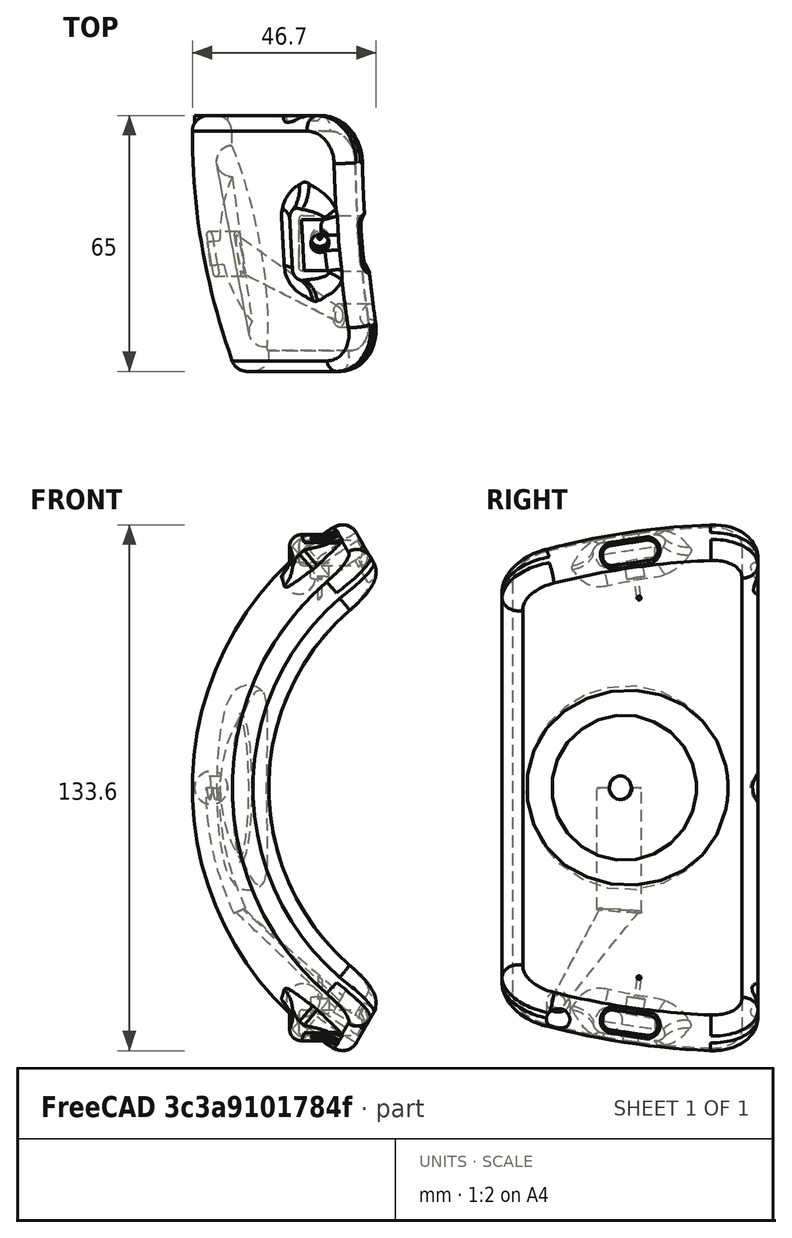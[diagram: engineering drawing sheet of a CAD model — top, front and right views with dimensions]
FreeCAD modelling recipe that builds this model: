
FCSTD DOCUMENT  (FreeCAD 0.17R13541 (Git))
Label: right_patch_backup
License: All rights reserved
LicenseURL: http://en.wikipedia.org/wiki/All_rights_reserved
objects: PartDesign::Fillet×12, Sketcher::SketchObject×11, PartDesign::Pocket×4, PartDesign::Mirrored×4, PartDesign::Revolution×1, PartDesign::Line×1, PartDesign::SubtractiveSphere×1, PartDesign::SubtractiveTorus×1, PartDesign::SubtractiveCylinder×1, PartDesign::AdditiveLoft×1, PartDesign::Plane×1, PartDesign::Body×1, PartDesign::Groove×1, PartDesign::SubtractiveLoft×1, PartDesign::Pad×1
note: 54 computed .brp shape members not serialized (recipe doc carries the construction recipe); baked Part::Feature solids carry a one-line shape summary decoded from their .brp

FEATURE [Sketcher::SketchObject] Sketch
  MapMode = 5
  Support = -> [XY_Plane]
  sketch-geometry (14):
    g0: LineSegment StartX=-68 StartY=0 StartZ=0 EndX=-58 EndY=0 EndZ=0
    g1: LineSegment StartX=-79 StartY=65 StartZ=0 EndX=-69 EndY=65 EndZ=0
    g2: Circle [constr] CenterX=-79 CenterY=65 CenterZ=0 NormalX=0 NormalY=0 NormalZ=1 AngleXU=0 Radius=1
    g3: Circle [constr] CenterX=-80 CenterY=32.5 CenterZ=0 NormalX=0 NormalY=0 NormalZ=1 AngleXU=0 Radius=1
    g4: Circle [constr] CenterX=-68 CenterY=0 CenterZ=0 NormalX=0 NormalY=0 NormalZ=1 AngleXU=0 Radius=1
    g5: BSplineCurve PolesCount=3 KnotsCount=2 Degree=2 IsPeriodic=0
    g6: GeomPoint [constr] X=-79 Y=65 Z=0
    g7: GeomPoint [constr] X=-68 Y=0 Z=0
    g8: Circle [constr] CenterX=-69 CenterY=65 CenterZ=0 NormalX=0 NormalY=0 NormalZ=1 AngleXU=0 Radius=1
    g9: Circle [constr] CenterX=-70 CenterY=32.5 CenterZ=0 NormalX=0 NormalY=0 NormalZ=1 AngleXU=0 Radius=1
    g10: Circle [constr] CenterX=-58 CenterY=0 CenterZ=0 NormalX=0 NormalY=0 NormalZ=1 AngleXU=0 Radius=1
    g11: BSplineCurve PolesCount=3 KnotsCount=2 Degree=2 IsPeriodic=0
    g12: GeomPoint [constr] X=-69 Y=65 Z=0
    g13: GeomPoint [constr] X=-58 Y=0 Z=0
  constraints (32):
    c: Horizontal(g0)
    c: Horizontal(g1)
    c: Coincident(g2,g1)
    c: Radius(g2) = 1
    c: Equal(g2,g3)
    c: Equal(g2,g4)
    c: Coincident(g4,g0)
    c: InternalAlignment(g2,g5)
    c: InternalAlignment(g3,g5)
    c: InternalAlignment(g4,g5)
    c: InternalAlignment(g6,g5)
    c: InternalAlignment(g7,g5)
    c: Coincident(g8,g1)
    c: Radius(g8) = 1
    c: Equal(g8,g9)
    c: Equal(g8,g10)
    c: Coincident(g10,g0)
    c: InternalAlignment(g8,g11)
    c: InternalAlignment(g9,g11)
    c: InternalAlignment(g10,g11)
    c: InternalAlignment(g12,g11)
    c: InternalAlignment(g13,g11)
    c: DistanceX(g1,g1) = 10
    c: DistanceX(g0,g0) = 10
    c: DistanceY(g0,g1) = 65
    c: DistanceY(g0,g-1) = 0
    c: DistanceY(g0,g9) = 32.5
    c: DistanceY(g0,g3) = 32.5
    c: DistanceX(g0,g-1) = 58
    c: DistanceX(g3,g9) = 10
    c: DistanceX(g9,g0) = 12
    c: DistanceX(g1,g0) = 11
FEATURE [PartDesign::Revolution] Revolution
  Angle = 120
  Axis = (0,1,0)
  Base = (0,0,0)
  Midplane = true
  Profile = -> Sketch
  ReferenceAxis = -> Sketch [V_Axis]
FEATURE [Sketcher::SketchObject] Sketch001
  MapMode = 5
  Support = -> [XY_Plane]
  sketch-geometry (5):
    g0: ArcOfCircle CenterX=-74.7751 CenterY=34.7178 CenterZ=0 NormalX=0 NormalY=0 NormalZ=1 AngleXU=0 Radius=0.75 StartAngle=0.174533 EndAngle=3.31613
    g1: ArcOfCircle CenterX=-73.0386 CenterY=24.8698 CenterZ=0 NormalX=0 NormalY=0 NormalZ=1 AngleXU=0 Radius=0.75 StartAngle=3.31613 EndAngle=6.45772
    g2: LineSegment StartX=-75.5137 StartY=34.5876 StartZ=0 EndX=-73.7772 EndY=24.7395 EndZ=0
    g3: LineSegment StartX=-74.0365 StartY=34.8481 StartZ=0 EndX=-72.3 EndY=25 EndZ=0
    g4: LineSegment [constr] StartX=17.7 StartY=33.8377 StartZ=0 EndX=17.7 EndY=-7.32293 EndZ=0
  constraints (12):
    c: Tangent(g0,g3) = 1.5708
    c: Tangent(g0,g2) = -1.5708
    c: Tangent(g2,g1) = -1.5708
    c: Tangent(g3,g1) = 1.5708
    c: Equal(g0,g1)
    c: Angle(g-1,g3) = 1.74533
    c: Distance(g1,g0) = 10
    c: Distance(g0,g0) = 1.5
    c: DistanceX(g1,g-1) = 72.3
    c: DistanceY(g-1,g1) = 25
    c: Vertical(g4)
    c: DistanceX(g1,g4) = 90
FEATURE [Sketcher::SketchObject] Sketch002
  MapMode = 5
  Placement = pos=(0,23,0) rot=(1,0,0;1.5708rad)
  sketch-geometry (5):
    g0: LineSegment StartX=-54 StartY=63 StartZ=0 EndX=-40 EndY=63 EndZ=0
    g1: LineSegment [constr] StartX=-40 StartY=63 StartZ=0 EndX=-40 EndY=45 EndZ=0
    g2: LineSegment [constr] StartX=-40 StartY=45 StartZ=0 EndX=-54 EndY=45 EndZ=0
    g3: LineSegment StartX=-54 StartY=45 StartZ=0 EndX=-54 EndY=63 EndZ=0
    g4: LineSegment StartX=-54 StartY=45 StartZ=0 EndX=-40 EndY=63 EndZ=0
  constraints (14):
    c: Coincident(g0,g1)
    c: Coincident(g1,g2)
    c: Coincident(g2,g3)
    c: Coincident(g3,g0)
    c: Horizontal(g0)
    c: Horizontal(g2)
    c: Vertical(g1)
    c: Vertical(g3)
    c: DistanceY(g1,g0) = 18
    c: DistanceX(g0,g0) = 14
    c: DistanceX(g1,g-1) = 40
    c: DistanceY(g-1,g0) = 63
    c: Coincident(g4,g0)
    c: Coincident(g4,g2)
FEATURE [Sketcher::SketchObject] Sketch003
  MapMode = 5
  Placement = pos=(0,0,0) rot=(0.57735,0.57735,0.57735;2.0944rad)
  Support = -> [YZ_Plane]
  sketch-geometry (4):
    g0: ArcOfCircle CenterX=28.0189 CenterY=59 CenterZ=0 NormalX=0 NormalY=0 NormalZ=1 AngleXU=0 Radius=2.57832 StartAngle=1.71915 EndAngle=4.86074
    g1: ArcOfCircle CenterX=37.0189 CenterY=60.3451 CenterZ=0 NormalX=0 NormalY=0 NormalZ=1 AngleXU=0 Radius=2.57832 StartAngle=4.86074 EndAngle=8.00233
    g2: LineSegment StartX=28.4 StartY=56.45 StartZ=0 EndX=37.4 EndY=57.7951 EndZ=0
    g3: LineSegment StartX=27.6378 StartY=61.55 StartZ=0 EndX=36.6378 EndY=62.8951 EndZ=0
  constraints (10):
    c: Tangent(g0,g3) = 1.5708
    c: Tangent(g0,g2) = -1.5708
    c: Tangent(g2,g1) = -1.5708
    c: Tangent(g3,g1) = 1.5708
    c: Equal(g0,g1)
    c: DistanceY(g1,g1) = 5.1
    c: DistanceX(g0,g1) = 9
    c: DistanceX(g-1,g0) = 28.4
    c: DistanceY(g-1,g0) = 59
    c: Angle(g3,g-1) = -0.148353
FEATURE [Sketcher::SketchObject] Sketch004
  MapMode = 5
  Placement = pos=(0,42,0) rot=(1,0,0;1.5708rad)
  sketch-geometry (5):
    g0: LineSegment StartX=-54 StartY=65.8 StartZ=0 EndX=-40 EndY=65.8 EndZ=0
    g1: LineSegment [constr] StartX=-40 StartY=65.8 StartZ=0 EndX=-40 EndY=47.8 EndZ=0
    g2: LineSegment [constr] StartX=-40 StartY=47.8 StartZ=0 EndX=-54 EndY=47.8 EndZ=0
    g3: LineSegment StartX=-54 StartY=47.8 StartZ=0 EndX=-54 EndY=65.8 EndZ=0
    g4: LineSegment StartX=-54 StartY=47.8 StartZ=0 EndX=-40 EndY=65.8 EndZ=0
  constraints (14):
    c: Coincident(g0,g1)
    c: Coincident(g1,g2)
    c: Coincident(g2,g3)
    c: Coincident(g3,g0)
    c: Horizontal(g0)
    c: Horizontal(g2)
    c: Vertical(g1)
    c: Vertical(g3)
    c: DistanceY(g1,g0) = 18
    c: DistanceX(g0,g0) = 14
    c: DistanceX(g1,g-1) = 40
    c: DistanceY(g-1,g0) = 65.8
    c: Coincident(g4,g0)
    c: Coincident(g4,g2)
FEATURE [PartDesign::Line] DatumLine
  AttacherType = Attacher::AttachEngineLine
  AttachmentOffset = pos=(44,0,0) rot=(0,1,0;0.174533rad)
  MapMode = 29
  Placement = pos=(0,44,0) rot=(0.510274,0.60812,0.60812;2.19793rad)
  Support = -> [X_Axis]
FEATURE [PartDesign::SubtractiveSphere] Sphere
  Angle1 = -90
  Angle2 = 90
  Angle3 = 360
  AttacherType = Attacher::AttachEngine3D
  AttachmentOffset = pos=(0,0,-36) rot=(0,0,1;0rad)
  BaseFeature = -> Revolution
  MapMode = 2
  Placement = pos=(-35.4531,37.7487,0) rot=(0.510274,0.60812,0.60812;2.19793rad)
  Radius = 36.5
  Support = -> [DatumLine]
FEATURE [PartDesign::SubtractiveTorus] Torus
  Angle1 = -180
  Angle2 = 180
  Angle3 = 360
  AttacherType = Attacher::AttachEngine3D
  AttachmentOffset = pos=(0,0,-64.5) rot=(0,0,1;0rad)
  BaseFeature = -> Sphere
  MapMode = 2
  Placement = pos=(-63.5201,32.7997,0) rot=(0.510274,0.60812,0.60812;2.19793rad)
  Radius1 = 22
  Radius2 = 4
  Support = -> [DatumLine]
FEATURE [PartDesign::SubtractiveCylinder] Cylinder
  Angle = 360
  AttacherType = Attacher::AttachEngine3D
  AttachmentOffset = pos=(0,0,-74) rot=(0,0,1;0rad)
  BaseFeature = -> Torus
  Height = 9
  MapMode = 2
  Placement = pos=(-72.8758,31.15,0) rot=(0.510274,0.60812,0.60812;2.19793rad)
  Radius = 3
  Support = -> [DatumLine]
FEATURE [PartDesign::Fillet] Fillet
  Base = -> Cylinder [Edge10,Edge9,Edge7,Edge6]
  BaseFeature = -> Cylinder
  Placement = pos=(-72.8758,31.15,0) rot=(0.510274,0.60812,0.60812;2.19793rad)
  Radius = 12
FEATURE [PartDesign::Fillet] Fillet001
  Base = -> Fillet [Edge1,Edge13]
  BaseFeature = -> Fillet
  Placement = pos=(-72.8758,31.15,0) rot=(0.510274,0.60812,0.60812;2.19793rad)
  Radius = 4
FEATURE [PartDesign::AdditiveLoft] AdditiveLoft
  BaseFeature = -> Fillet001
  Closed = false
  Placement = pos=(-72.8758,31.15,0) rot=(0.510274,0.60812,0.60812;2.19793rad)
  Profile = -> Sketch002
  Ruled = false
  Sections = -> [Sketch004]
FEATURE [PartDesign::Plane] DatumPlane
  AttachmentOffset = pos=(0,0,70) rot=(0,0,1;0rad)
  MapMode = 2
  Placement = pos=(0,0,70) rot=(0,0,1;0rad)
  Support = -> [XY_Plane]
FEATURE [Sketcher::SketchObject] Sketch015
  MapMode = 5
  Placement = pos=(0,0,70) rot=(0,0,1;0rad)
  Support = -> [DatumPlane]
  sketch-geometry (1):
    g0: Circle CenterX=-47 CenterY=32 CenterZ=0 NormalX=0 NormalY=0 NormalZ=1 AngleXU=0 Radius=2.55
  constraints (3):
    c: Radius(g0) = 2.55
    c: DistanceY(g-1,g0) = 32
    c: DistanceX(g0,g-1) = 47
FEATURE [PartDesign::Body] Body
  Group = -> [Sketch,Revolution,Sphere,DatumLine,Torus,Sketch001,Cylinder,Sketch002,Fillet,Fillet001,Sketch003,Sketch004,AdditiveLoft,Fillet015,Pocket,DatumPlane,Sketch015,Pocket006,Fillet002,Fillet003,Fillet004,Fillet005,Mirrored,Mirrored001,Mirrored002,Fillet014,Fillet011,Fillet008,Fillet009,Fillet010,Groove,Sketch010,Pocket004,Sketch011,Sketch012,SubtractiveLoft,Sketch013,Pad,Sketch014,Pocket005,Mirrored003]
  Origin = -> Origin
  Tip = -> Mirrored003
FEATURE [PartDesign::Pocket] Pocket
  BaseFeature = -> Fillet015
  Length = 52
  Length2 = 100
  Placement = pos=(-72.8758,31.15,0) rot=(0.510274,0.60812,0.60812;2.19793rad)
  Profile = -> Sketch003
  Type = 0
FEATURE [PartDesign::Fillet] Fillet002
  Base = -> Pocket006 [Edge82]
  BaseFeature = -> Pocket006
  Placement = pos=(-72.8758,31.15,0) rot=(0.510274,0.60812,0.60812;2.19793rad)
  Radius = 1
FEATURE [PartDesign::Fillet] Fillet003
  Base = -> Fillet002 [Edge61,Edge82,Edge83]
  BaseFeature = -> Fillet002
  Placement = pos=(-72.8758,31.15,0) rot=(0.510274,0.60812,0.60812;2.19793rad)
  Radius = 3
FEATURE [PartDesign::Fillet] Fillet004
  Base = -> Fillet003 [Edge9]
  BaseFeature = -> Fillet003
  Placement = pos=(-72.8758,31.15,0) rot=(0.510274,0.60812,0.60812;2.19793rad)
  Radius = 7.5
FEATURE [PartDesign::Fillet] Fillet005
  Base = -> Fillet004 [Edge48]
  BaseFeature = -> Fillet004
  Placement = pos=(-72.8758,31.15,0) rot=(0.510274,0.60812,0.60812;2.19793rad)
  Radius = 0.5
FEATURE [PartDesign::Mirrored] Mirrored
  BaseFeature = -> Fillet005
  MirrorPlane = -> XY_Plane
  Originals = -> [AdditiveLoft]
  Placement = pos=(-72.8758,31.15,0) rot=(0.510274,0.60812,0.60812;2.19793rad)
FEATURE [PartDesign::Mirrored] Mirrored001
  BaseFeature = -> Mirrored
  MirrorPlane = -> XY_Plane
  Originals = -> [Pocket]
  Placement = pos=(-72.8758,31.15,0) rot=(0.510274,0.60812,0.60812;2.19793rad)
FEATURE [PartDesign::Fillet] Fillet008
  Base = -> Fillet011 [Edge6]
  BaseFeature = -> Fillet011
  Placement = pos=(-74.8078,29.8527,2.20324e-05) rot=(0.706297,0.047857,0.706296;3.23724rad)
  Radius = 7.5
FEATURE [PartDesign::Fillet] Fillet009
  Base = -> Fillet008 [Edge49]
  BaseFeature = -> Fillet008
  Placement = pos=(-74.8078,29.8527,2.20324e-05) rot=(0.706297,0.047857,0.706296;3.23724rad)
  Radius = 1.5
FEATURE [PartDesign::Fillet] Fillet010
  Base = -> Fillet009 [Edge249]
  BaseFeature = -> Fillet009
  Placement = pos=(-74.8078,29.8527,2.20324e-05) rot=(0.706297,0.047857,0.706296;3.23724rad)
  Radius = 0.5
FEATURE [PartDesign::Groove] Groove
  Angle = 25
  Axis = (0,1,0)
  Base = (0,0,0)
  BaseFeature = -> Fillet010
  Placement = pos=(-74.8078,29.8527,2.20324e-05) rot=(0.706297,0.047857,0.706296;3.23724rad)
  Profile = -> Sketch001
  ReferenceAxis = -> Sketch001 [V_Axis]
  Reversed = true
FEATURE [PartDesign::Fillet] Fillet011
  Base = -> Fillet014 [Edge100,Edge59,Edge57,Edge58,Edge101]
  BaseFeature = -> Fillet014
  Placement = pos=(-74.8078,29.8527,2.20324e-05) rot=(0.706297,0.047857,0.706296;3.23724rad)
  Radius = 3
FEATURE [PartDesign::Fillet] Fillet014
  Base = -> Mirrored002 [Edge181]
  BaseFeature = -> Mirrored002
  Placement = pos=(-74.8078,29.8527,2.20324e-05) rot=(0.706297,0.047857,0.706296;3.23724rad)
  Radius = 1
FEATURE [PartDesign::Mirrored] Mirrored002
  BaseFeature = -> Mirrored001
  MirrorPlane = -> XY_Plane
  Placement = pos=(-62.6655,14.4247,-1.686e-09) rot=(0.556096,0.587689,0.587689;2.12657rad)
FEATURE [Sketcher::SketchObject] Sketch010
  MapMode = 5
  Placement = pos=(-18.7515,29.8257,-32.4785) rot=(0.866025,-2e-06,0.5;3.1416rad)
  Support = -> [Groove]
  sketch-geometry (1):
    g0: Circle CenterX=-30.5085 CenterY=15.6064 CenterZ=0 NormalX=0 NormalY=0 NormalZ=1 AngleXU=0 Radius=3
  constraints (1):
    c: Radius(g0) = 3
FEATURE [PartDesign::Pocket] Pocket004
  BaseFeature = -> Groove
  Length = 9
  Length2 = 100
  Placement = pos=(-74.8078,29.8527,2.20324e-05) rot=(0.706297,0.047857,0.706296;3.23724rad)
  Profile = -> Sketch010
  Type = 0
FEATURE [Sketcher::SketchObject] Sketch011
  MapMode = 5
  Placement = pos=(-26.5457,29.8257,-27.9785) rot=(0.866025,-2e-06,0.5;3.1416rad)
  Support = -> [Pocket004]
  sketch-geometry (1):
    g0: Circle CenterX=-30.4793 CenterY=15.6052 CenterZ=0 NormalX=0 NormalY=0 NormalZ=1 AngleXU=0 Radius=1.84995
FEATURE [Sketcher::SketchObject] Sketch012
  MapMode = 5
  Placement = pos=(-61.4467,29.8527,-28.6531) rot=(0.210233,-0.237767,-0.948298;1.50086rad)
  Support = -> [Pocket004]
  sketch-geometry (5):
    g0: Ellipse CenterX=-0.623981 CenterY=-6.08723 CenterZ=0 NormalX=0 NormalY=0 NormalZ=1 MajorRadius=5.00319 MinorRadius=0.669168 AngleXU=0.0564247
    g1: LineSegment [constr] StartX=4.37125 StartY=-5.80508 StartZ=0 EndX=-5.61921 EndY=-6.36939 EndZ=0
    g2: LineSegment [constr] StartX=-0.661718 StartY=-5.41913 StartZ=0 EndX=-0.586243 EndY=-6.75534 EndZ=0
    g3: GeomPoint X=4.32637 Y=-5.80762 Z=0
    g4: GeomPoint X=-5.57433 Y=-6.36685 Z=0
  constraints (1):
    c: InternalAlignment(g1-g4 -> g0) x4
FEATURE [PartDesign::SubtractiveLoft] SubtractiveLoft
  BaseFeature = -> Pocket004
  Closed = false
  Placement = pos=(-74.8078,29.8527,2.20324e-05) rot=(0.706297,0.047857,0.706296;3.23724rad)
  Profile = -> Sketch011
  Ruled = false
  Sections = -> [Sketch012]
FEATURE [Sketcher::SketchObject] Sketch013
  MapMode = 5
  Placement = pos=(-74.8078,65,2.20324e-05) rot=(-0.577351,-0.57735,-0.57735;2.09439rad)
  Support = -> [SubtractiveLoft]
  sketch-geometry (3):
    g0: Circle CenterX=-53.9992 CenterY=23.9428 CenterZ=0 NormalX=0 NormalY=0 NormalZ=1 AngleXU=0 Radius=4.22785
    g1: Circle CenterX=0 CenterY=0.539508 CenterZ=0 NormalX=0 NormalY=0 NormalZ=1 AngleXU=0 Radius=4.22063
    g2: Circle CenterX=53.2365 CenterY=22.8948 CenterZ=0 NormalX=0 NormalY=0 NormalZ=1 AngleXU=0 Radius=4.03213
  constraints (1):
    c: PointOnObject(g1,g-2)
FEATURE [PartDesign::Pad] Pad
  BaseFeature = -> SubtractiveLoft
  Length = 4.5
  Length2 = 100
  Placement = pos=(-74.8078,29.8527,2.20324e-05) rot=(0.706297,0.047857,0.706296;3.23724rad)
  Profile = -> Sketch013
  Reversed = true
  Type = 0
FEATURE [Sketcher::SketchObject] Sketch014
  ExternalGeometry = -> [Pad]
  MapMode = 5
  Placement = pos=(-74.8078,21.9878,51.5285) rot=(0.086468,0.075376,-0.993399;1.4405rad)
  Support = -> [Pad]
  sketch-geometry (1):
    g0: Circle CenterX=-8.22449 CenterY=29.5233 CenterZ=0 NormalX=0 NormalY=0 NormalZ=1 AngleXU=0 Radius=0.5
  constraints (2):
    c: Coincident(g0,g-3)
    c: Radius(g0) = 0.5
FEATURE [PartDesign::Pocket] Pocket005
  BaseFeature = -> Pad
  Length = 5
  Length2 = 100
  Placement = pos=(-74.8078,29.8527,2.20324e-05) rot=(0.706297,0.047857,0.706296;3.23724rad)
  Profile = -> Sketch014
  Type = 2
FEATURE [PartDesign::Mirrored] Mirrored003
  BaseFeature = -> Pocket005
  MirrorPlane = -> XY_Plane
  Originals = -> [Pocket005]
  Placement = pos=(-74.8078,29.8527,2.20324e-05) rot=(0.706297,0.047857,0.706296;3.23724rad)
FEATURE [PartDesign::Pocket] Pocket006
  BaseFeature = -> Pocket
  Length = 16
  Length2 = 100
  Placement = pos=(-72.8758,31.15,0) rot=(0.510274,0.60812,0.60812;2.19793rad)
  Profile = -> Sketch015
  Type = 0
FEATURE [PartDesign::Fillet] Fillet015
  Base = -> Fillet003 [Edge4]
  BaseFeature = -> Fillet003
  Placement = pos=(-72.8758,31.15,0) rot=(0.510274,0.60812,0.60812;2.19793rad)
  Radius = 2
